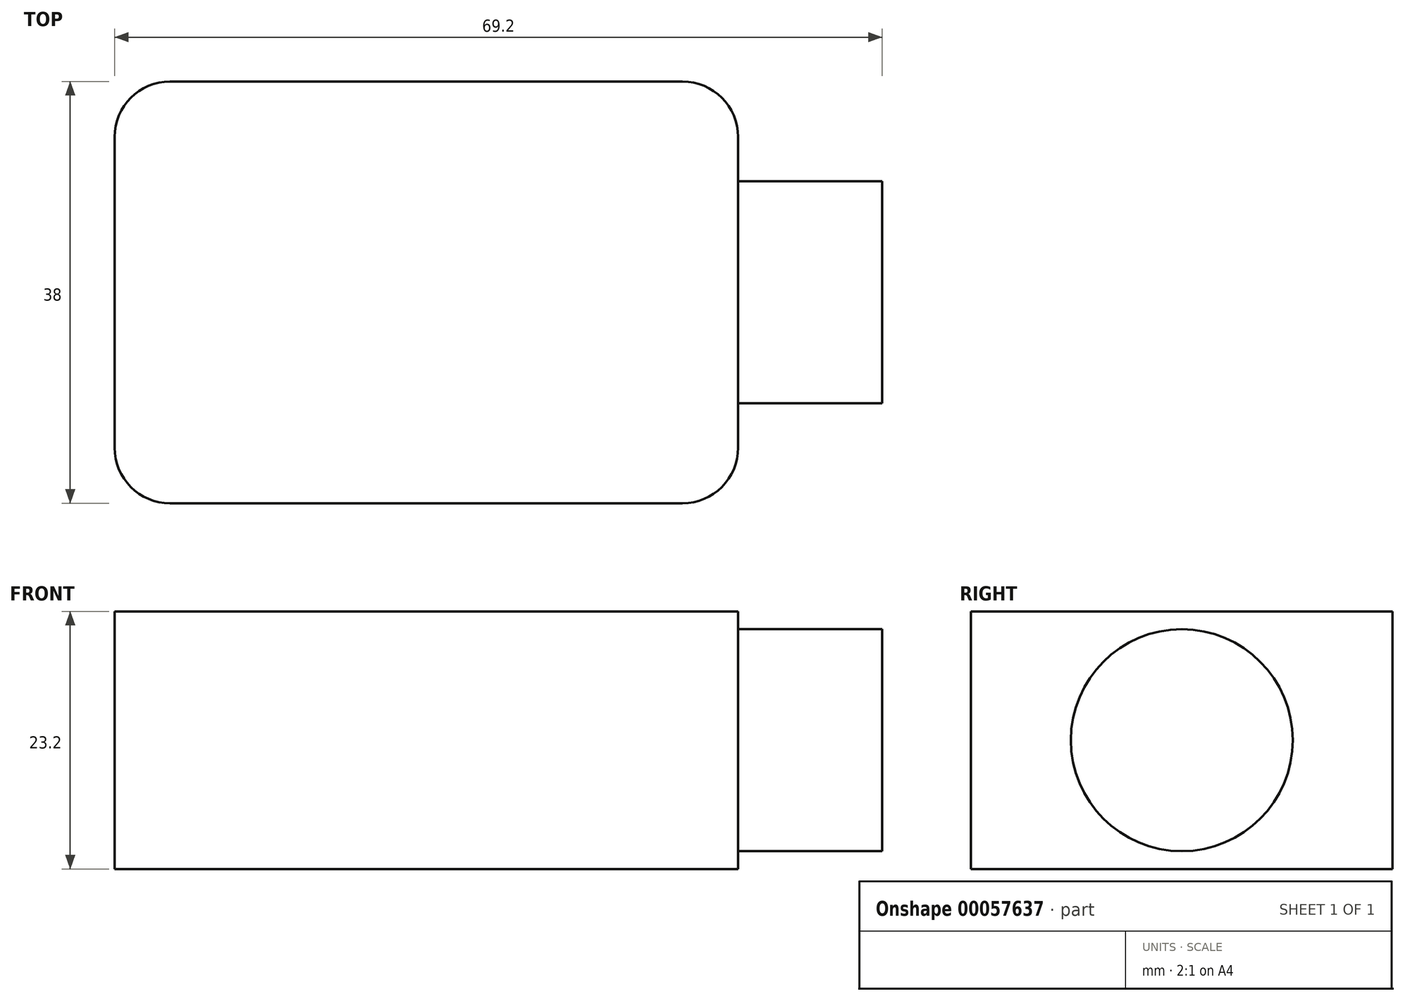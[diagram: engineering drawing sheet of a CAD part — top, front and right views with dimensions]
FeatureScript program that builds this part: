
annotation { "Feature Type Name" : "Feature", "Feature Type Description" : "" }
export const myFeature = defineFeature(function(context is Context, id is Id, definition is map)
    precondition{}
    {
        {
            var Q0;
            Q0=qCreatedBy(makeId("Top.planeOp"),FACE);
            var sketch = newSketch(context, id + "F0", { "sketchPlane" : qUnion([Q0])});
            skLineSegment(sketch, "E0.rect.bottom", {"start": v(-28.1, 19) * mm, "end": v(28.1, 19) * mm});
            skLineSegment(sketch, "E0.rect.top", {"start": v(-28.1, -19) * mm, "end": v(28.1, -19) * mm});
            skLineSegment(sketch, "E0.rect.left", {"start": v(-28.1, 19) * mm, "end": v(-28.1, -19) * mm});
            skLineSegment(sketch, "E0.rect.right", {"start": v(28.1, 19) * mm, "end": v(28.1, -19) * mm});
            skPoint(sketch, "E0.rect.middle", {"position": v(0, 0) * mm});
            skSolve(sketch);
        }
        {
            var Q0;
            Q0=makeQuery(id+"F0.imprint","IMPRINT",FACE,{"disambiguationData":[TD([[makeQuery(id+"F0.imprint","IMPRINT",EDGE,{"derivedFrom":sQuery(id+"F0.wireOp",EDGE,"E0.rect.bottom")}),-1.0]])]});
            extrude(context, id + "F1", {"entities" : qUnion([Q0]), "depth" : 23.2 * mm});
        }
        {
            var Q0;
            Q0=makeQuery(id+"F1.opExtrude","SWEPT_EDGE",EDGE,{"disambiguationData":[OSD([sQuery(id+"F0.wireOp",EDGE,"E0.rect.top"),sQuery(id+"F0.wireOp",EDGE,"E0.rect.right")])]});
            var Q1;
            Q1=makeQuery(id+"F1.opExtrude","SWEPT_EDGE",EDGE,{"disambiguationData":[OSD([sQuery(id+"F0.wireOp",EDGE,"E0.rect.bottom"),sQuery(id+"F0.wireOp",EDGE,"E0.rect.right")])]});
            var Q2;
            Q2=makeQuery(id+"F1.opExtrude","SWEPT_EDGE",EDGE,{"disambiguationData":[OSD([sQuery(id+"F0.wireOp",EDGE,"E0.rect.bottom"),sQuery(id+"F0.wireOp",EDGE,"E0.rect.left")])]});
            var Q3;
            Q3=makeQuery(id+"F1.opExtrude","SWEPT_EDGE",EDGE,{"disambiguationData":[OSD([sQuery(id+"F0.wireOp",EDGE,"E0.rect.top"),sQuery(id+"F0.wireOp",EDGE,"E0.rect.left")])]});
            fillet(context, id + "F2", {"entities" : qUnion([Q0, Q1, Q2, Q3]), "radius" : 5 * mm, "tangentPropagation" : true, "allowEdgeOverflow" : false});
        }
        {
            var Q0;
            Q0=makeQuery(id+"F1.opExtrude","SWEPT_FACE",FACE,{"disambiguationData":[OSD([sQuery(id+"F0.wireOp",EDGE,"E0.rect.right")])]});
            var sketch = newSketch(context, id + "F3", { "sketchPlane" : qUnion([Q0])});
            skCircle(sketch, "E1", {"center": v(0, 11.6) * mm, "radius": 10 * mm});
            skPoint(sketch, "E1.centerSnap0", {"position": v(0, 23.2) * mm});
            skPoint(sketch, "E1.centerSnap1", {"position": v(-14, 11.6) * mm});
            skSolve(sketch);
        }
        {
            var Q0;
            Q0 = qSketchRegion(id + "F3", true);
            extrude(context, id + "F4", {"entities" : qUnion([Q0]), "operationType" : NewBodyOperationType.ADD, "depth" : 13 * mm});
        }
    });
